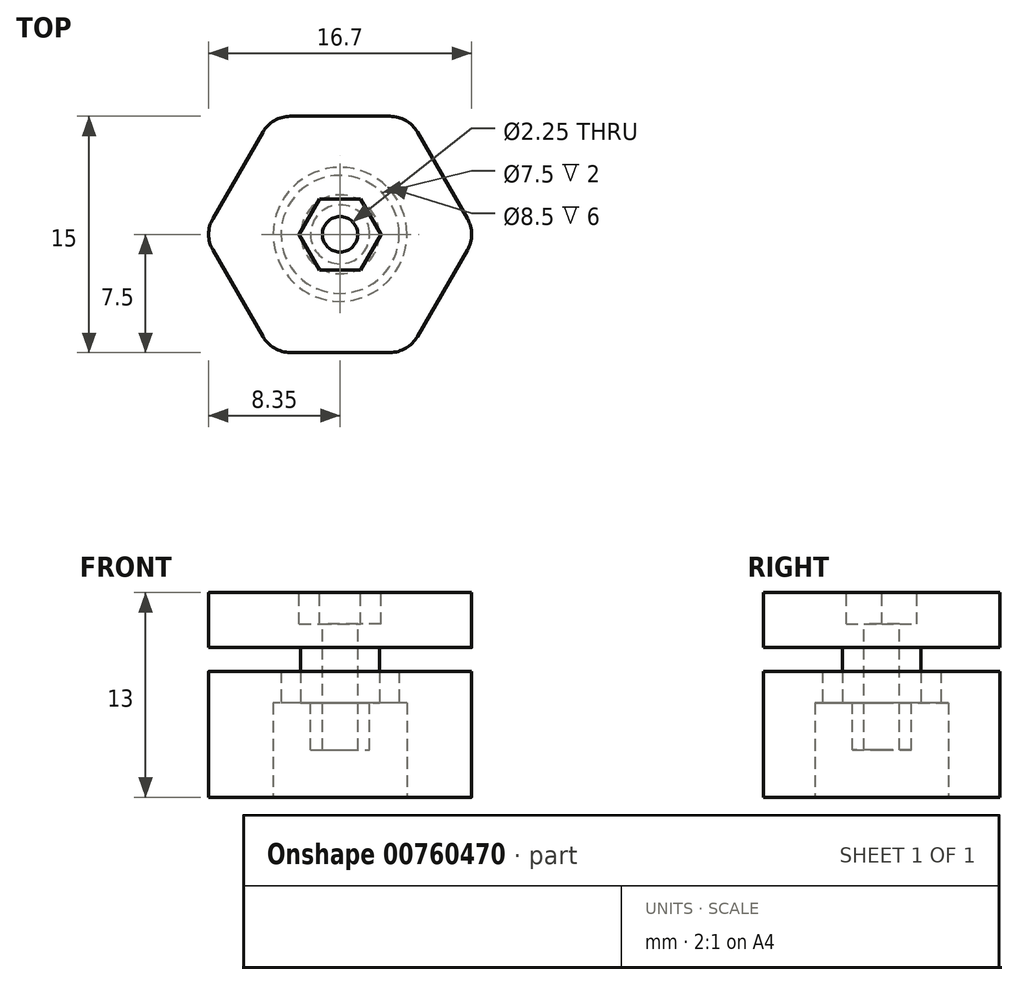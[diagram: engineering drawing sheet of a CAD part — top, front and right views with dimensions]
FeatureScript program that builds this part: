
annotation { "Feature Type Name" : "Feature", "Feature Type Description" : "" }
export const myFeature = defineFeature(function(context is Context, id is Id, definition is map)
    precondition{}
    {
        {
            var Q0;
            Q0=qCreatedBy(makeId("Top.planeOp"),FACE);
            var sketch = newSketch(context, id + "F0", { "sketchPlane" : qUnion([Q0])});
            skCircle(sketch, "E0", {"center": v(0, 0) * mm, "radius": 4.25 * mm});
            skCircle(sketch, "E1", {"center": v(0, 0) * mm, "radius": 3.75 * mm});
            skCircle(sketch, "E2.cCircle", {"center": v(0, 0) * mm, "radius": 7.5 * mm, "construction": true});
            skLineSegment(sketch, "E2.0", {"start": v(-4.33, 7.5) * mm, "end": v(4.33, 7.5) * mm});
            skLineSegment(sketch, "E2.1", {"start": v(4.33, 7.5) * mm, "end": v(8.66, 0) * mm});
            skLineSegment(sketch, "E2.2", {"start": v(8.66, 0) * mm, "end": v(4.33, -7.5) * mm});
            skLineSegment(sketch, "E2.3", {"start": v(4.33, -7.5) * mm, "end": v(-4.33, -7.5) * mm});
            skLineSegment(sketch, "E2.4", {"start": v(-4.33, -7.5) * mm, "end": v(-8.66, 0) * mm});
            skLineSegment(sketch, "E2.5", {"start": v(-8.66, 0) * mm, "end": v(-4.33, 7.5) * mm});
            skPoint(sketch, "E2.0.midPoint", {"position": v(0, 7.5) * mm});
            skSolve(sketch);
        }
        {
            var Q0;
            Q0=makeQuery(id+"F0.imprint","IMPRINT",FACE,{"disambiguationData":[TD([[makeQuery(id+"F0.imprint","IMPRINT",EDGE,{"derivedFrom":sQuery(id+"F0.wireOp",EDGE,"E0")}),-1.0]])]});
            var Q1;
            Q1=makeQuery(id+"F0.imprint","IMPRINT",FACE,{"disambiguationData":[TD([[makeQuery(id+"F0.imprint","IMPRINT",EDGE,{"derivedFrom":sQuery(id+"F0.wireOp",EDGE,"E0")}),1.0]])]});
            extrude(context, id + "F1", {"entities" : qUnion([Q0, Q1]), "depth" : 8 * mm, "offsetDistance" : 25 * mm});
        }
        {
            var Q0;
            Q0=makeQuery(id+"F0.imprint","IMPRINT",FACE,{"disambiguationData":[TD([[makeQuery(id+"F0.imprint","IMPRINT",EDGE,{"derivedFrom":sQuery(id+"F0.wireOp",EDGE,"E0")}),1.0]])]});
            extrude(context, id + "F2", {"entities" : qUnion([Q0]), "operationType" : NewBodyOperationType.REMOVE, "depth" : 6 * mm, "offsetDistance" : 25 * mm});
        }
        {
            var Q0;
            Q0=makeQuery(id+"F2.boolean.opBoolean","COPY",FACE,{"derivedFrom":makeQuery(id+"F2.opExtrude","CAP_FACE",FACE,{"disambiguationData":[OSD([sQuery(id+"F0.wireOp",EDGE,"E0"),sQuery(id+"F0.wireOp",EDGE,"E1")])],"isStart":false})});
            var sketch = newSketch(context, id + "F3", { "sketchPlane" : qUnion([Q0])});
            skCircle(sketch, "E3", {"center": v(0, 0) * mm, "radius": 2.5 * mm});
            skSolve(sketch);
        }
        {
            var Q0;
            Q0=makeQuery(id+"F3.imprint","IMPRINT",FACE,{"disambiguationData":[TD([[makeQuery(id+"F3.imprint","IMPRINT",EDGE,{"derivedFrom":sQuery(id+"F3.wireOp",EDGE,"E3")}),1.0]])]});
            extrude(context, id + "F4", {"entities" : qUnion([Q0]), "oppositeDirection" : true, "depth" : 3.5 * mm, "offsetDistance" : 25 * mm});
        }
        {
            var Q0;
            Q0=makeQuery(id+"F4.opExtrude","CAP_FACE",FACE,{"disambiguationData":[OSD([sQuery(id+"F3.wireOp",EDGE,"E3"),sQuery(id+"F3.wireOp",EDGE,"KjZoWoZm-BD7A-KjsF-ZKL1-DKTP2S4fCj8n")])],"isStart":false});
            var sketch = newSketch(context, id + "F5", { "sketchPlane" : qUnion([Q0])});
            skCircle(sketch, "E4.cCircle", {"center": v(0, 0) * mm, "radius": 7.5 * mm, "construction": true});
            skLineSegment(sketch, "E4.0", {"start": v(-4.33, 7.5) * mm, "end": v(4.33, 7.5) * mm});
            skLineSegment(sketch, "E4.1", {"start": v(4.33, 7.5) * mm, "end": v(8.66, 0) * mm});
            skLineSegment(sketch, "E4.2", {"start": v(8.66, 0) * mm, "end": v(4.33, -7.5) * mm});
            skLineSegment(sketch, "E4.3", {"start": v(4.33, -7.5) * mm, "end": v(-4.33, -7.5) * mm});
            skLineSegment(sketch, "E4.4", {"start": v(-4.33, -7.5) * mm, "end": v(-8.66, 0) * mm});
            skLineSegment(sketch, "E4.5", {"start": v(-8.66, 0) * mm, "end": v(-4.33, 7.5) * mm});
            skPoint(sketch, "E4.0.midPoint", {"position": v(0, 7.5) * mm});
            skSolve(sketch);
        }
        {
            var Q0;
            Q0=makeQuery(id+"F5.imprint","IMPRINT",FACE,{"disambiguationData":[TD([[makeQuery(id+"F5.imprint","IMPRINT",EDGE,{"derivedFrom":sQuery(id+"F5.wireOp",EDGE,"E4.0")}),-1.0]])]});
            var Q1;
            Q1=makeQuery(id+"F5.imprint","IMPRINT",FACE,{"disambiguationData":[TD([[makeQuery(id+"F5.imprint","IMPRINT",EDGE,{"derivedFrom":makeQuery(id+"F4.opExtrude","CAP_EDGE",EDGE,{"disambiguationData":[OSD([sQuery(id+"F3.wireOp",EDGE,"E3")])],"isStart":false})}),-1.0]])]});
            extrude(context, id + "F6", {"entities" : qUnion([Q0, Q1]), "operationType" : NewBodyOperationType.ADD, "depth" : 3.5 * mm, "offsetDistance" : 25 * mm});
        }
        {
            var Q0;
            Q0=makeQuery(id+"F6.opExtrude","CAP_FACE",FACE,{"disambiguationData":[OSD([sQuery(id+"F5.wireOp",EDGE,"E4.0"),sQuery(id+"F5.wireOp",EDGE,"E4.1"),sQuery(id+"F5.wireOp",EDGE,"E4.2"),sQuery(id+"F5.wireOp",EDGE,"E4.3"),sQuery(id+"F5.wireOp",EDGE,"E4.4"),sQuery(id+"F5.wireOp",EDGE,"E4.5")])],"isStart":false});
            var sketch = newSketch(context, id + "F7", { "sketchPlane" : qUnion([Q0])});
            skCircle(sketch, "E5", {"center": v(0, 0) * mm, "radius": 1.13 * mm});
            skCircle(sketch, "E6.cCircle", {"center": v(0, 0) * mm, "radius": 2.25 * mm, "construction": true});
            skLineSegment(sketch, "E6.0", {"start": v(-1.3, 2.25) * mm, "end": v(1.3, 2.25) * mm});
            skLineSegment(sketch, "E6.1", {"start": v(1.3, 2.25) * mm, "end": v(2.6, 0) * mm});
            skLineSegment(sketch, "E6.2", {"start": v(2.6, 0) * mm, "end": v(1.3, -2.25) * mm});
            skLineSegment(sketch, "E6.3", {"start": v(1.3, -2.25) * mm, "end": v(-1.3, -2.25) * mm});
            skLineSegment(sketch, "E6.4", {"start": v(-1.3, -2.25) * mm, "end": v(-2.6, 0) * mm});
            skLineSegment(sketch, "E6.5", {"start": v(-2.6, 0) * mm, "end": v(-1.3, 2.25) * mm});
            skPoint(sketch, "E6.0.midPoint", {"position": v(0, 2.25) * mm});
            skSolve(sketch);
        }
        {
            var Q0;
            Q0=makeQuery(id+"F7.imprint","IMPRINT",FACE,{"disambiguationData":[TD([[makeQuery(id+"F7.imprint","IMPRINT",EDGE,{"derivedFrom":sQuery(id+"F7.wireOp",EDGE,"E5")}),-1.0]])]});
            extrude(context, id + "F8", {"entities" : qUnion([Q0]), "operationType" : NewBodyOperationType.REMOVE, "oppositeDirection" : true, "depth" : 2 * mm, "offsetDistance" : 25 * mm});
        }
        {
            var Q0;
            Q0=makeQuery(id+"F1.opExtrude","SWEPT_EDGE",EDGE,{"disambiguationData":[OSD([sQuery(id+"F0.wireOp",EDGE,"E2.4"),sQuery(id+"F0.wireOp",EDGE,"E2.5")])]});
            var Q1;
            Q1=makeQuery(id+"F6.opExtrude","SWEPT_EDGE",EDGE,{"disambiguationData":[OSD([sQuery(id+"F5.wireOp",EDGE,"E4.4"),sQuery(id+"F5.wireOp",EDGE,"E4.5")])]});
            var Q2;
            Q2=makeQuery(id+"F6.opExtrude","SWEPT_EDGE",EDGE,{"disambiguationData":[OSD([sQuery(id+"F5.wireOp",EDGE,"E4.0"),sQuery(id+"F5.wireOp",EDGE,"E4.5")])]});
            var Q3;
            Q3=makeQuery(id+"F1.opExtrude","SWEPT_EDGE",EDGE,{"disambiguationData":[OSD([sQuery(id+"F0.wireOp",EDGE,"E2.0"),sQuery(id+"F0.wireOp",EDGE,"E2.5")])]});
            var Q4;
            Q4=makeQuery(id+"F1.opExtrude","SWEPT_EDGE",EDGE,{"disambiguationData":[OSD([sQuery(id+"F0.wireOp",EDGE,"E2.3"),sQuery(id+"F0.wireOp",EDGE,"E2.4")])]});
            var Q5;
            Q5=makeQuery(id+"F6.opExtrude","SWEPT_EDGE",EDGE,{"disambiguationData":[OSD([sQuery(id+"F5.wireOp",EDGE,"E4.3"),sQuery(id+"F5.wireOp",EDGE,"E4.4")])]});
            var Q6;
            Q6=makeQuery(id+"F1.opExtrude","SWEPT_EDGE",EDGE,{"disambiguationData":[OSD([sQuery(id+"F0.wireOp",EDGE,"E2.2"),sQuery(id+"F0.wireOp",EDGE,"E2.3")])]});
            var Q7;
            Q7=makeQuery(id+"F1.opExtrude","SWEPT_EDGE",EDGE,{"disambiguationData":[OSD([sQuery(id+"F0.wireOp",EDGE,"E2.1"),sQuery(id+"F0.wireOp",EDGE,"E2.2")])]});
            var Q8;
            Q8=makeQuery(id+"F1.opExtrude","SWEPT_EDGE",EDGE,{"disambiguationData":[OSD([sQuery(id+"F0.wireOp",EDGE,"E2.0"),sQuery(id+"F0.wireOp",EDGE,"E2.1")])]});
            var Q9;
            Q9=makeQuery(id+"F6.opExtrude","SWEPT_EDGE",EDGE,{"disambiguationData":[OSD([sQuery(id+"F5.wireOp",EDGE,"E4.0"),sQuery(id+"F5.wireOp",EDGE,"E4.1")])]});
            var Q10;
            Q10=makeQuery(id+"F6.opExtrude","SWEPT_EDGE",EDGE,{"disambiguationData":[OSD([sQuery(id+"F5.wireOp",EDGE,"E4.1"),sQuery(id+"F5.wireOp",EDGE,"E4.2")])]});
            var Q11;
            Q11=makeQuery(id+"F6.opExtrude","SWEPT_EDGE",EDGE,{"disambiguationData":[OSD([sQuery(id+"F5.wireOp",EDGE,"E4.2"),sQuery(id+"F5.wireOp",EDGE,"E4.3")])]});
            fillet(context, id + "F9", {"entities" : qUnion([Q0, Q1, Q2, Q3, Q4, Q5, Q6, Q7, Q8, Q9, Q10, Q11]), "radius" : 2 * mm, "tangentPropagation" : true, "allowEdgeOverflow" : false});
        }
        {
            var Q0;
            Q0=makeQuery(id+"F4.opExtrude","CAP_FACE",FACE,{"disambiguationData":[OSD([sQuery(id+"F3.wireOp",EDGE,"E3")])],"isStart":true});
            var sketch = newSketch(context, id + "F10", { "sketchPlane" : qUnion([Q0])});
            skCircle(sketch, "E7", {"center": v(0, 0) * mm, "radius": 1.88 * mm});
            skSolve(sketch);
        }
        {
            var Q0;
            Q0 = qSketchRegion(id + "F10", true);
            extrude(context, id + "F11", {"entities" : qUnion([Q0]), "operationType" : NewBodyOperationType.ADD, "depth" : 3 * mm, "offsetDistance" : 25 * mm});
        }
        {
            var Q0;
            Q0=makeQuery(id+"F7.imprint","IMPRINT",FACE,{"disambiguationData":[TD([[makeQuery(id+"F7.imprint","IMPRINT",EDGE,{"derivedFrom":sQuery(id+"F7.wireOp",EDGE,"E5")}),1.0]])]});
            extrude(context, id + "F12", {"entities" : qUnion([Q0]), "operationType" : NewBodyOperationType.REMOVE, "endBound" : BoundingType.THROUGH_ALL, "oppositeDirection" : true, "depth" : 25 * mm, "offsetDistance" : 25 * mm});
        }
    });
